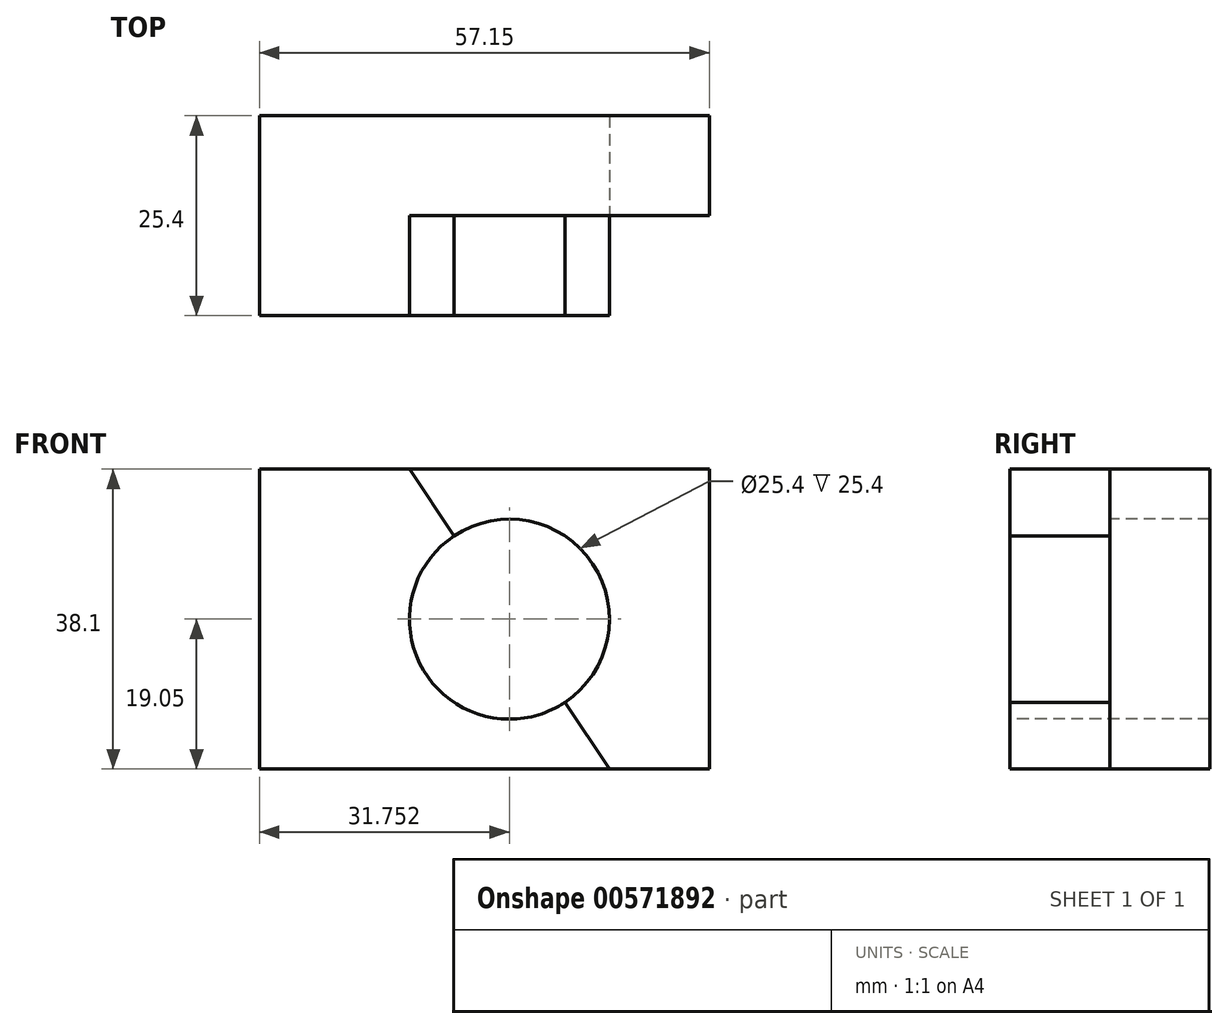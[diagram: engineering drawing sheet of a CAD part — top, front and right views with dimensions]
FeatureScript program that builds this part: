
annotation { "Feature Type Name" : "Feature", "Feature Type Description" : "" }
export const myFeature = defineFeature(function(context is Context, id is Id, definition is map)
    precondition{}
    {
        {
            var Q0;
            Q0=qCreatedBy(makeId("Front.planeOp"),FACE);
            var sketch = newSketch(context, id + "F0", { "sketchPlane" : qUnion([Q0])});
            skLineSegment(sketch, "E0.bottom", {"start": v(-28.54, 0) * mm, "end": v(28.61, 0) * mm});
            skLineSegment(sketch, "E0.top", {"start": v(-28.54, 38.1) * mm, "end": v(28.61, 38.1) * mm});
            skLineSegment(sketch, "E0.left", {"start": v(-28.54, 0) * mm, "end": v(-28.54, 38.1) * mm});
            skLineSegment(sketch, "E0.right", {"start": v(28.61, 0) * mm, "end": v(28.61, 38.1) * mm});
            skSolve(sketch);
        }
        {
            var Q0;
            Q0=makeQuery(id+"F0.imprint","IMPRINT",FACE,{"disambiguationData":[TD([[makeQuery(id+"F0.imprint","IMPRINT",EDGE,{"derivedFrom":sQuery(id+"F0.wireOp",EDGE,"E0.bottom")}),1.0]])]});
            extrude(context, id + "F1", {"entities" : qUnion([Q0]), "depth" : 25.4 * mm, "offsetDistance" : 25.4 * mm});
        }
        {
            var Q0;
            Q0=makeQuery(id+"F1.opExtrude","SWEPT_FACE",FACE,{"disambiguationData":[OSD([sQuery(id+"F0.wireOp",EDGE,"E0.top")])]});
            var sketch = newSketch(context, id + "F2", { "sketchPlane" : qUnion([Q0])});
            skLineSegment(sketch, "E1", {"start": v(28.61, -12.7) * mm, "end": v(15.91, -12.7) * mm});
            skLineSegment(sketch, "E2", {"start": v(15.91, -12.7) * mm, "end": v(15.91, -25.4) * mm});
            skSolve(sketch);
        }
        {
            var Q0;
            {var subQ0=sQuery(id+"F2.wireOp",EDGE,"E1");Q0=makeQuery(id+"F2.imprint","IMPRINT",FACE,{"disambiguationData":[TD([[makeQuery(id+"F2.imprint","IMPRINT",EDGE,{"derivedFrom":subQ0}),1.0]])]});}
            extrude(context, id + "F3", {"entities" : qUnion([Q0]), "operationType" : NewBodyOperationType.REMOVE, "endBound" : BoundingType.THROUGH_ALL, "oppositeDirection" : true, "depth" : 25.4 * mm, "offsetDistance" : 25.4 * mm});
        }
        {
            var Q0;
            Q0=makeQuery(id+"F1.opExtrude","CAP_FACE",FACE,{"disambiguationData":[OSD([sQuery(id+"F0.wireOp",EDGE,"E0.bottom"),sQuery(id+"F0.wireOp",EDGE,"E0.top"),sQuery(id+"F0.wireOp",EDGE,"E0.left"),sQuery(id+"F0.wireOp",EDGE,"E0.right")])],"isStart":false});
            var sketch = newSketch(context, id + "F4", { "sketchPlane" : qUnion([Q0])});
            skLineSegment(sketch, "E3", {"start": v(-9.49, 38.1) * mm, "end": v(15.91, 0) * mm});
            skSolve(sketch);
        }
        {
            var Q0;
            {var subQ0=sQuery(id+"F4.wireOp",EDGE,"E3");Q0=makeQuery(id+"F4.imprint","IMPRINT",FACE,{"disambiguationData":[TD([[makeQuery(id+"F4.imprint","IMPRINT",EDGE,{"derivedFrom":subQ0}),1.0]])]});}
            extrude(context, id + "F5", {"entities" : qUnion([Q0]), "operationType" : NewBodyOperationType.REMOVE, "oppositeDirection" : true, "depth" : 12.7 * mm, "offsetDistance" : 25.4 * mm});
        }
        {
            var Q0;
            Q0=makeQuery(id+"F1.opExtrude","CAP_FACE",FACE,{"disambiguationData":[OSD([sQuery(id+"F0.wireOp",EDGE,"E0.bottom"),sQuery(id+"F0.wireOp",EDGE,"E0.top"),sQuery(id+"F0.wireOp",EDGE,"E0.left"),sQuery(id+"F0.wireOp",EDGE,"E0.right")])],"isStart":false});
            var sketch = newSketch(context, id + "F6", { "sketchPlane" : qUnion([Q0])});
            skCircle(sketch, "E4", {"center": v(3.21, 19.05) * mm, "radius": 12.7 * mm});
            skSolve(sketch);
        }
        {
            var Q0;
            {var subQ0=sQuery(id+"F6.wireOp",EDGE,"E4");var subQ1=makeQuery(id+"F5.boolean.opBoolean","COPY",EDGE,{"derivedFrom":makeQuery(id+"F5.opExtrude","CAP_EDGE",EDGE,{"disambiguationData":[OSD([sQuery(id+"F4.wireOp",EDGE,"E3")])],"isStart":true})});var subQ2=makeQuery(id+"F6.imprint","INTERSECT",VERTEX,{"disambiguationData":[OD(0.0)],"derivedFrom":[subQ1,subQ0]});Q0=makeQuery(id+"F6.imprint","IMPRINT",FACE,{"disambiguationData":[TD([[makeQuery(id+"F6.imprint","IMPRINT",EDGE,{"disambiguationData":[TD([[subQ2,-1.0]])],"derivedFrom":subQ0}),1.0]])]});}
            var Q1;
            {var subQ0=sQuery(id+"F6.wireOp",EDGE,"E4");var subQ1=makeQuery(id+"F5.boolean.opBoolean","COPY",EDGE,{"derivedFrom":makeQuery(id+"F5.opExtrude","CAP_EDGE",EDGE,{"disambiguationData":[OSD([sQuery(id+"F4.wireOp",EDGE,"E3")])],"isStart":true})});var subQ2=makeQuery(id+"F6.imprint","INTERSECT",VERTEX,{"disambiguationData":[OD(0.0)],"derivedFrom":[subQ1,subQ0]});Q1=makeQuery(id+"F6.imprint","IMPRINT",FACE,{"disambiguationData":[TD([[makeQuery(id+"F6.imprint","IMPRINT",EDGE,{"disambiguationData":[TD([[subQ2,1.0]])],"derivedFrom":subQ0}),1.0]])]});}
            extrude(context, id + "F7", {"entities" : qUnion([Q0, Q1]), "operationType" : NewBodyOperationType.REMOVE, "endBound" : BoundingType.THROUGH_ALL, "oppositeDirection" : true, "depth" : 25.4 * mm, "offsetDistance" : 25.4 * mm});
        }
    });
